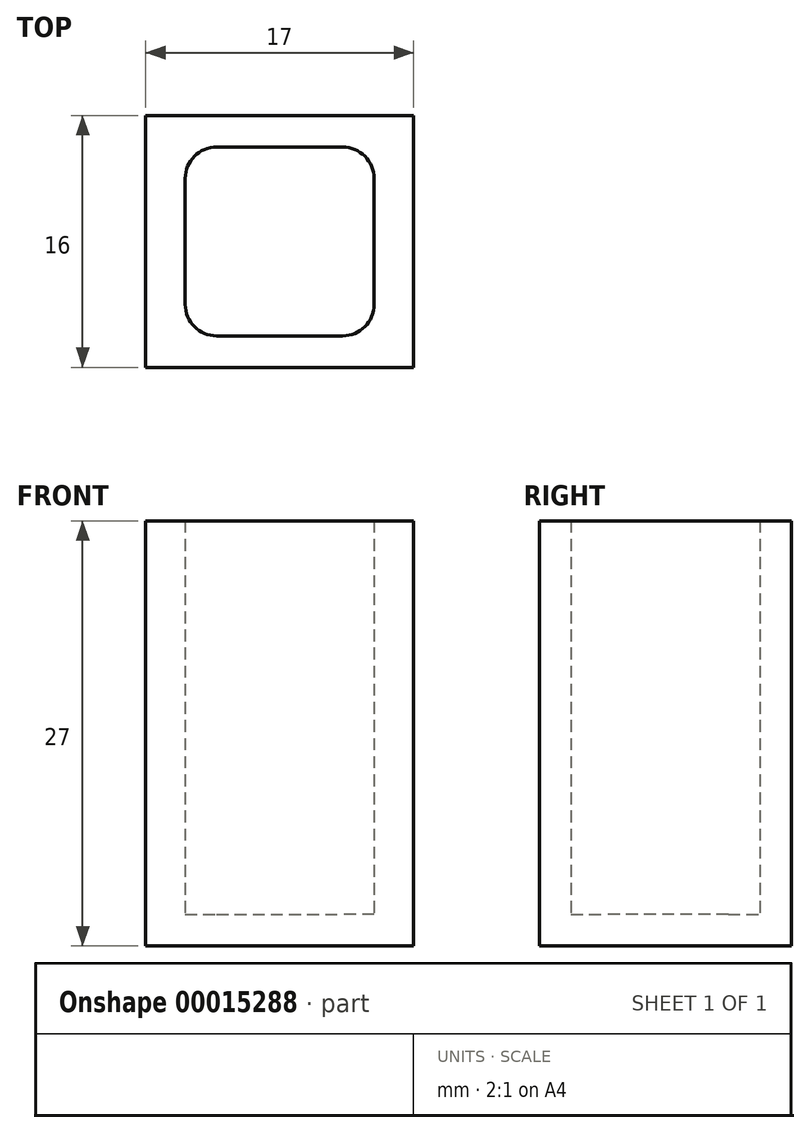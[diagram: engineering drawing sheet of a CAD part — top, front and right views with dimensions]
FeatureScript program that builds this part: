
annotation { "Feature Type Name" : "Feature", "Feature Type Description" : "" }
export const myFeature = defineFeature(function(context is Context, id is Id, definition is map)
    precondition{}
    {
        {
            var Q0;
            Q0=qCreatedBy(makeId("Top.planeOp"),FACE);
            var sketch = newSketch(context, id + "F0", { "sketchPlane" : qUnion([Q0])});
            skLineSegment(sketch, "E0.bottom", {"start": v(2, 0) * mm, "end": v(10, 0) * mm});
            skLineSegment(sketch, "E0.top", {"start": v(2, -12) * mm, "end": v(10, -12) * mm});
            skLineSegment(sketch, "E0.left", {"start": v(0, -2) * mm, "end": v(0, -10) * mm});
            skLineSegment(sketch, "E0.right", {"start": v(12, -2) * mm, "end": v(12, -10) * mm});
            skPoint(sketch, "E1.visualSharp", {"position": v(0, 0) * mm});
            skArc(sketch, "E1.filletArc", {"start": v(2, 0) * mm, "mid": v(0.59, -0.59) * mm, "end": v(0, -2) * mm});
            skPoint(sketch, "E2.visualSharp", {"position": v(12, 0) * mm});
            skArc(sketch, "E2.filletArc", {"start": v(12, -2) * mm, "mid": v(11.41, -0.59) * mm, "end": v(10, 0) * mm});
            skPoint(sketch, "E3.visualSharp", {"position": v(12, -12) * mm});
            skArc(sketch, "E3.filletArc", {"start": v(10, -12) * mm, "mid": v(11.41, -11.41) * mm, "end": v(12, -10) * mm});
            skPoint(sketch, "E4.visualSharp", {"position": v(0, -12) * mm});
            skArc(sketch, "E4.filletArc", {"start": v(0, -10) * mm, "mid": v(0.59, -11.41) * mm, "end": v(2, -12) * mm});
            skLineSegment(sketch, "E5.bottom", {"start": v(-2.5, 2) * mm, "end": v(14.5, 2) * mm});
            skLineSegment(sketch, "E5.top", {"start": v(-2.5, -14) * mm, "end": v(14.5, -14) * mm});
            skLineSegment(sketch, "E5.left", {"start": v(-2.5, 2) * mm, "end": v(-2.5, -14) * mm});
            skLineSegment(sketch, "E5.right", {"start": v(14.5, 2) * mm, "end": v(14.5, -14) * mm});
            skSolve(sketch);
        }
        {
            var Q0;
            Q0=makeQuery(id+"F0.imprint","IMPRINT",FACE,{"disambiguationData":[TD([[makeQuery(id+"F0.imprint","IMPRINT",EDGE,{"derivedFrom":sQuery(id+"F0.wireOp",EDGE,"E0.bottom")}),1.0]])]});
            var Q1;
            Q1=makeQuery(id+"F0.imprint","IMPRINT",FACE,{"disambiguationData":[TD([[makeQuery(id+"F0.imprint","IMPRINT",EDGE,{"derivedFrom":sQuery(id+"F0.wireOp",EDGE,"E0.bottom")}),-1.0]])]});
            extrude(context, id + "F1", {"entities" : qUnion([Q0, Q1]), "oppositeDirection" : true, "depth" : 2 * mm});
        }
        {
            var Q0;
            Q0=makeQuery(id+"F0.imprint","IMPRINT",FACE,{"disambiguationData":[TD([[makeQuery(id+"F0.imprint","IMPRINT",EDGE,{"derivedFrom":sQuery(id+"F0.wireOp",EDGE,"E0.bottom")}),1.0]])]});
            extrude(context, id + "F2", {"entities" : qUnion([Q0]), "operationType" : NewBodyOperationType.ADD, "depth" : 25 * mm});
        }
    });
